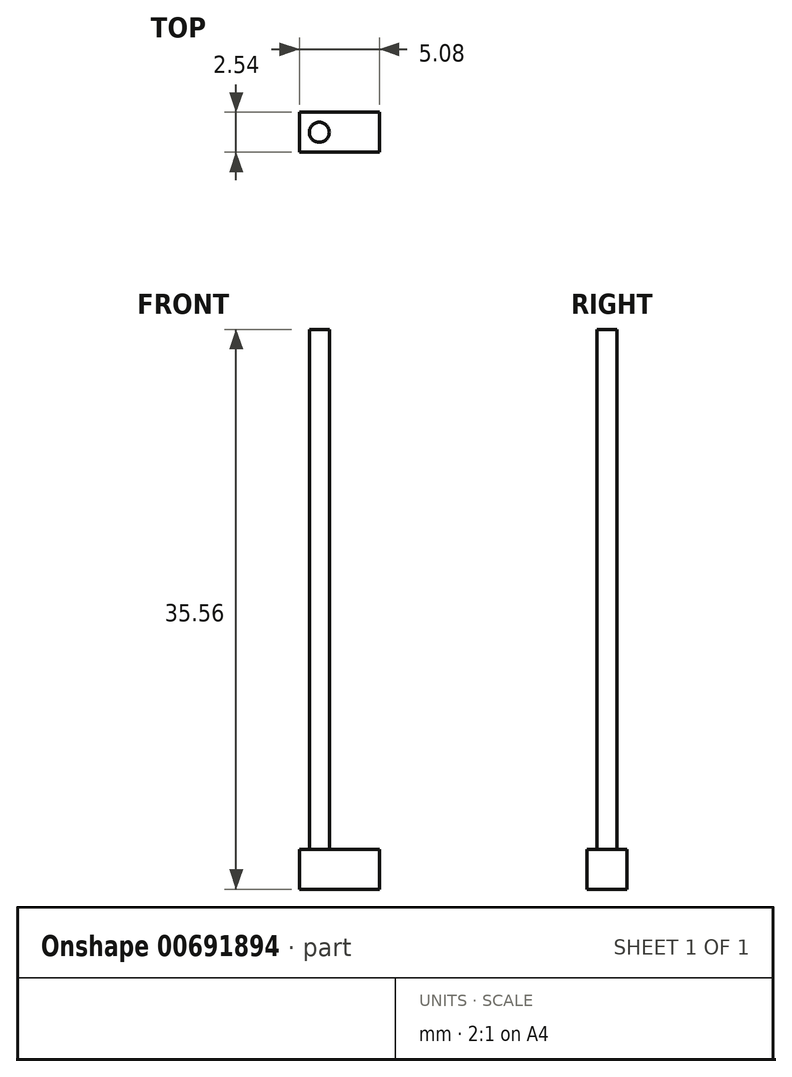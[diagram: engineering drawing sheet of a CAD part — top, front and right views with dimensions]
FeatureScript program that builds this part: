
annotation { "Feature Type Name" : "Feature", "Feature Type Description" : "" }
export const myFeature = defineFeature(function(context is Context, id is Id, definition is map)
    precondition{}
    {
        {
            var Q0;
            Q0=qCreatedBy(makeId("Top.planeOp"),FACE);
            var sketch = newSketch(context, id + "F0", { "sketchPlane" : qUnion([Q0])});
            skLineSegment(sketch, "E0.bottom", {"start": v(0, 0) * mm, "end": v(5.08, 0) * mm});
            skLineSegment(sketch, "E0.top", {"start": v(0, -2.54) * mm, "end": v(5.08, -2.54) * mm});
            skLineSegment(sketch, "E0.left", {"start": v(0, 0) * mm, "end": v(0, -2.54) * mm});
            skLineSegment(sketch, "E0.right", {"start": v(5.08, 0) * mm, "end": v(5.08, -2.54) * mm});
            skSolve(sketch);
        }
        {
            var Q0;
            Q0=makeQuery(id+"F0.imprint","IMPRINT",FACE,{"disambiguationData":[TD([[makeQuery(id+"F0.imprint","IMPRINT",EDGE,{"derivedFrom":sQuery(id+"F0.wireOp",EDGE,"E0.bottom")}),-1.0]])]});
            extrude(context, id + "F1", {"entities" : qUnion([Q0]), "depth" : 2.54 * mm, "offsetDistance" : 25.4 * mm});
        }
        {
            var Q0;
            Q0=makeQuery(id+"F1.opExtrude","CAP_FACE",FACE,{"disambiguationData":[OSD([sQuery(id+"F0.wireOp",EDGE,"E0.bottom"),sQuery(id+"F0.wireOp",EDGE,"E0.top"),sQuery(id+"F0.wireOp",EDGE,"E0.left"),sQuery(id+"F0.wireOp",EDGE,"E0.right")])],"isStart":false});
            var sketch = newSketch(context, id + "F2", { "sketchPlane" : qUnion([Q0])});
            skCircle(sketch, "E1", {"center": v(1.27, -1.27) * mm, "radius": 0.64 * mm});
            skSolve(sketch);
        }
        {
            var Q0;
            {var subQ0=sQuery(id+"F2.wireOp",EDGE,"E1");var subQ1=makeQuery(id+"F2.imprint","INTERSECT",VERTEX,{"derivedFrom":[makeQuery(id+"F1.opExtrude","CAP_EDGE",EDGE,{"disambiguationData":[OSD([sQuery(id+"F0.wireOp",EDGE,"E0.left")])],"isStart":false}),subQ0]});Q0=makeQuery(id+"F2.imprint","IMPRINT",FACE,{"disambiguationData":[TD([[makeQuery(id+"F2.imprint","IMPRINT",EDGE,{"disambiguationData":[TD([[subQ1,1.0]])],"derivedFrom":subQ0}),1.0]])]});}
            extrude(context, id + "F3", {"entities" : qUnion([Q0]), "operationType" : NewBodyOperationType.ADD, "depth" : 33.02 * mm, "offsetDistance" : 25.4 * mm});
        }
    });
